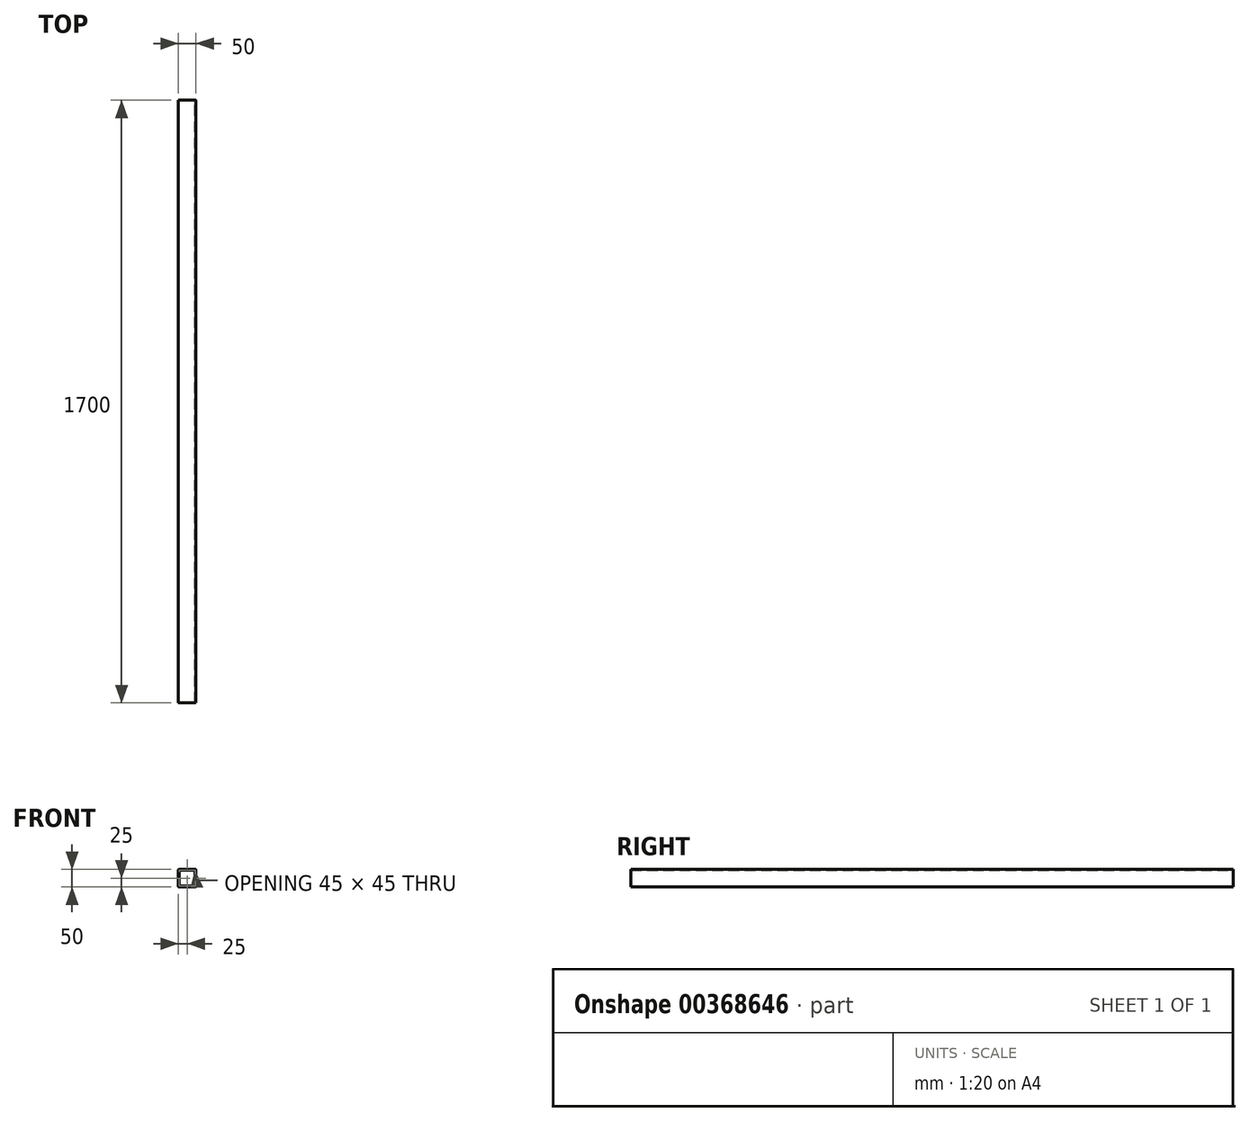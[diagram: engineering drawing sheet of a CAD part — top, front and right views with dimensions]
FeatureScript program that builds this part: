
annotation { "Feature Type Name" : "Feature", "Feature Type Description" : "" }
export const myFeature = defineFeature(function(context is Context, id is Id, definition is map)
    precondition{}
    {
        {
            var Q0;
            Q0=qCreatedBy(makeId("Front.planeOp"),FACE);
            var sketch = newSketch(context, id + "F0", { "sketchPlane" : qUnion([Q0])});
            skLineSegment(sketch, "E0.bottom", {"start": v(23, 25) * mm, "end": v(-23, 25) * mm});
            skLineSegment(sketch, "E0.top", {"start": v(23, -25) * mm, "end": v(-23, -25) * mm});
            skLineSegment(sketch, "E0.left", {"start": v(25, 23) * mm, "end": v(25, -23) * mm});
            skLineSegment(sketch, "E0.right", {"start": v(-25, 23) * mm, "end": v(-25, -23) * mm});
            skPoint(sketch, "E0.middle", {"position": v(0, 0) * mm});
            skLineSegment(sketch, "E1.bottom", {"start": v(20.5, 22.5) * mm, "end": v(-20.5, 22.5) * mm});
            skLineSegment(sketch, "E1.top", {"start": v(20.5, -22.5) * mm, "end": v(-20.5, -22.5) * mm});
            skLineSegment(sketch, "E1.left", {"start": v(22.5, 20.5) * mm, "end": v(22.5, -20.5) * mm});
            skLineSegment(sketch, "E1.right", {"start": v(-22.5, 20.5) * mm, "end": v(-22.5, -20.5) * mm});
            skPoint(sketch, "E2.visualSharp", {"position": v(-25, 25) * mm});
            skArc(sketch, "E2.filletArc", {"start": v(-23, 25) * mm, "mid": v(-24.41, 24.41) * mm, "end": v(-25, 23) * mm});
            skPoint(sketch, "E3.visualSharp", {"position": v(25, 25) * mm});
            skArc(sketch, "E3.filletArc", {"start": v(25, 23) * mm, "mid": v(24.41, 24.41) * mm, "end": v(23, 25) * mm});
            skPoint(sketch, "E4.visualSharp", {"position": v(22.5, 22.5) * mm});
            skArc(sketch, "E4.filletArc", {"start": v(22.5, 20.5) * mm, "mid": v(21.91, 21.91) * mm, "end": v(20.5, 22.5) * mm});
            skPoint(sketch, "E5.visualSharp", {"position": v(-22.5, 22.5) * mm});
            skArc(sketch, "E5.filletArc", {"start": v(-20.5, 22.5) * mm, "mid": v(-21.91, 21.91) * mm, "end": v(-22.5, 20.5) * mm});
            skPoint(sketch, "E6.visualSharp", {"position": v(-22.5, -22.5) * mm});
            skArc(sketch, "E6.filletArc", {"start": v(-22.5, -20.5) * mm, "mid": v(-21.91, -21.91) * mm, "end": v(-20.5, -22.5) * mm});
            skPoint(sketch, "E7.visualSharp", {"position": v(-25, -25) * mm});
            skArc(sketch, "E7.filletArc", {"start": v(-25, -23) * mm, "mid": v(-24.41, -24.41) * mm, "end": v(-23, -25) * mm});
            skPoint(sketch, "E8.visualSharp", {"position": v(22.5, -22.5) * mm});
            skArc(sketch, "E8.filletArc", {"start": v(20.5, -22.5) * mm, "mid": v(21.91, -21.91) * mm, "end": v(22.5, -20.5) * mm});
            skPoint(sketch, "E9.visualSharp", {"position": v(25, -25) * mm});
            skArc(sketch, "E9.filletArc", {"start": v(23, -25) * mm, "mid": v(24.41, -24.41) * mm, "end": v(25, -23) * mm});
            skSolve(sketch);
        }
        {
            var Q0;
            Q0=qSketchRegion(id+"F0",true);
            extrude(context, id + "F1", {"entities" : qUnion([Q0]), "endBound" : BoundingType.SYMMETRIC, "depth" : 1700 * mm});
        }
    });
